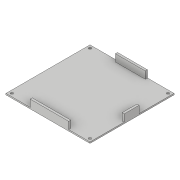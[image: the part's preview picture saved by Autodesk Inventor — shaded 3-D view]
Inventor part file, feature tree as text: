
AUTODESK INVENTOR PART (.ipt)
format: ipt  version: 2017 (Build 210142000, 142)  size: 118,272 bytes
history: native  units: in
note: dims shown in document units (in); Inventor stores cm internally (conversion verified against a paired STEP export)
features: extrude x2, sketch x2
ambient origin geometry x8: Origin, YZ Plane, XZ Plane, XY Plane, X Axis, Y Axis, Z Axis, Center Point
bodies: Solid1 (feature_tree)
feature tree (4):
  extrude  "Extrusion1"  Depth=3.937in
  extrude  "Extrusion2"  Depth=0.335in
  sketch  "Sketch1"  dims[d0=3.937in d1=3.937in]
  sketch  "Sketch2"  dims[d2=0.125in d3=0.125in d4=0.125in d5=0.125in d6=0.14in d7=0.14in d8=0.14in d9=0.14in d10=0.0625in d11=0.0in d12=0.1in d13=0.1in d14=0.1in d15=0.0in d16=0.0in d17=1.0in d18=1.8in d19=0.7in d20=1.4in d21=1.6in d22=1.25in d23=0.335in d24=0.0in]
